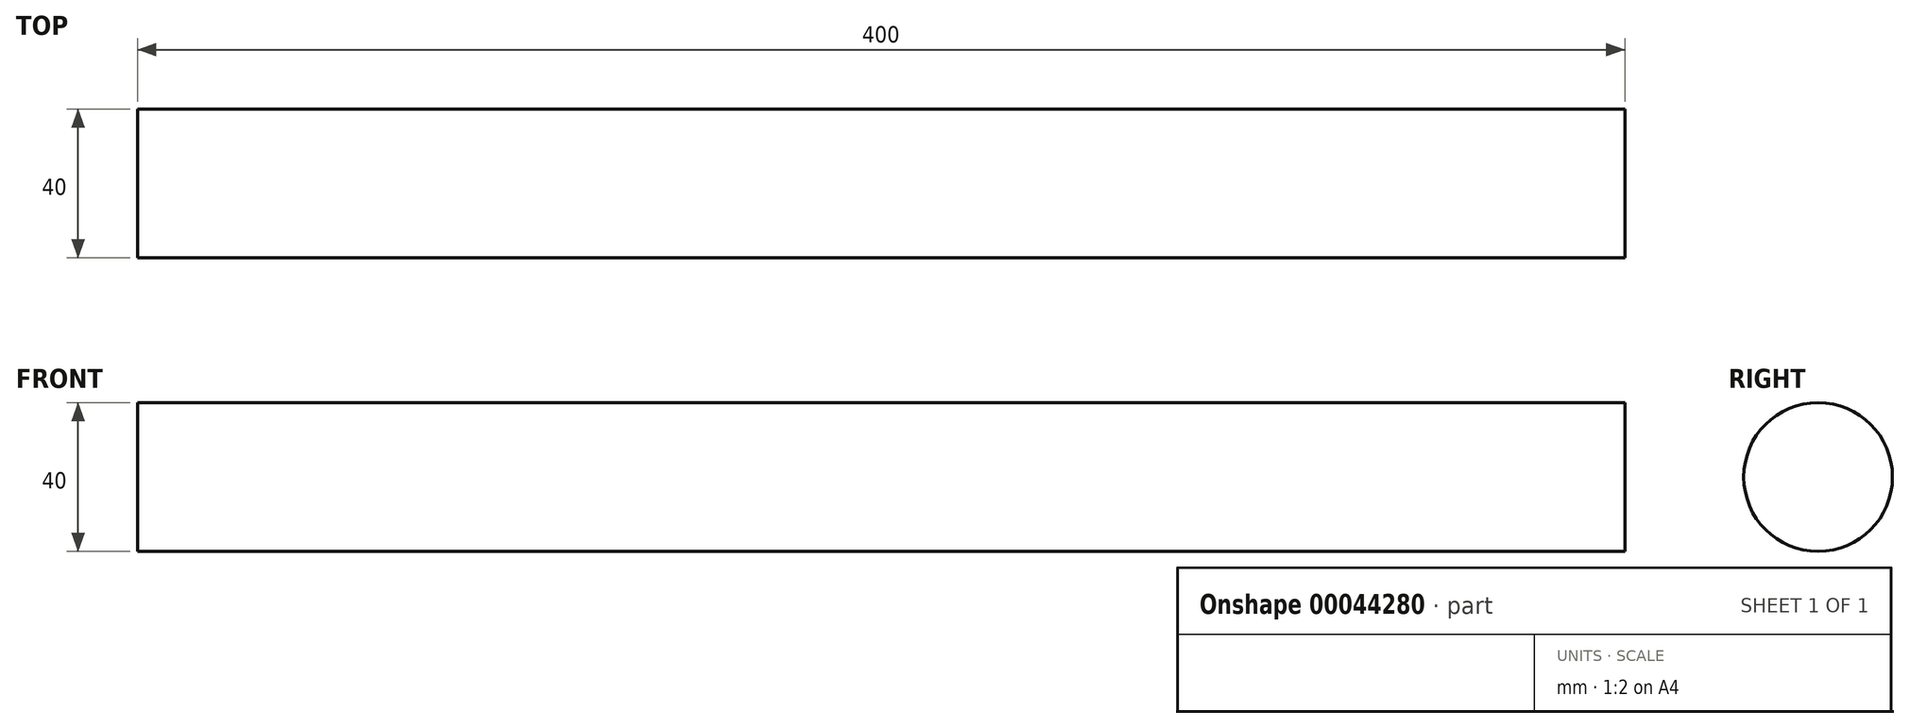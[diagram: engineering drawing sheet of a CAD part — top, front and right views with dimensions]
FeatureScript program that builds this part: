
annotation { "Feature Type Name" : "Feature", "Feature Type Description" : "" }
export const myFeature = defineFeature(function(context is Context, id is Id, definition is map)
    precondition{}
    {
        {
            var Q0;
            Q0=qCreatedBy(makeId("Right.planeOp"),FACE);
            var sketch = newSketch(context, id + "F0", { "sketchPlane" : qUnion([Q0])});
            skCircle(sketch, "E0", {"center": v(0, 0) * mm, "radius": 20 * mm});
            skSolve(sketch);
        }
        {
            var Q0;
            Q0=makeQuery(id+"F0.imprint","IMPRINT",FACE,{"disambiguationData":[TD([[makeQuery(id+"F0.imprint","IMPRINT",EDGE,{"derivedFrom":sQuery(id+"F0.wireOp",EDGE,"E0")}),1.0]])]});
            extrude(context, id + "F1", {"entities" : qUnion([Q0]), "depth" : 400 * mm});
        }
    });
